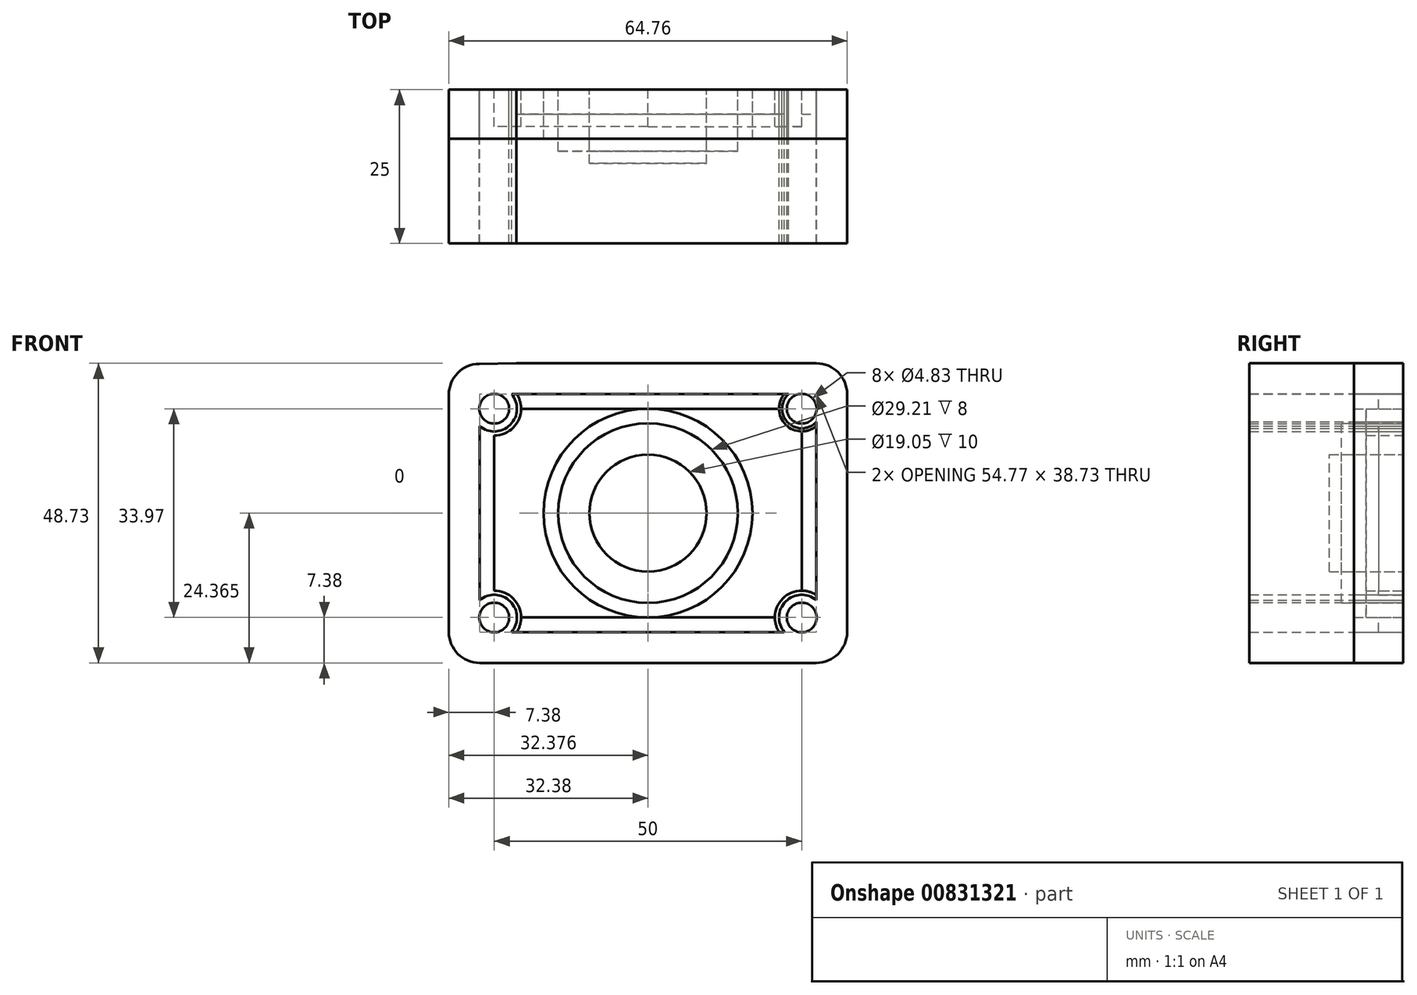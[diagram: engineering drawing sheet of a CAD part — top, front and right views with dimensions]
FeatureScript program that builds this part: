
annotation { "Feature Type Name" : "Feature", "Feature Type Description" : "" }
export const myFeature = defineFeature(function(context is Context, id is Id, definition is map)
    precondition{}
    {
        {
            var Q0;
            Q0=qCreatedBy(makeId("Front.planeOp"),FACE);
            var sketch = newSketch(context, id + "F0", { "sketchPlane" : qUnion([Q0])});
            skCircle(sketch, "E0", {"center": v(25, 0.52) * mm, "radius": 9.53 * mm});
            skCircle(sketch, "E1", {"center": v(25, 0.52) * mm, "radius": 14.6 * mm});
            skCircle(sketch, "E2", {"center": v(25, 0.52) * mm, "radius": 16.98 * mm});
            skLineSegment(sketch, "E3", {"start": v(25, 17.5) * mm, "end": v(46.8, 17.5) * mm});
            skLineSegment(sketch, "E4", {"start": v(25, 17.5) * mm, "end": v(4.37, 17.5) * mm});
            skLineSegment(sketch, "E5", {"start": v(25, -16.46) * mm, "end": v(46.31, -16.46) * mm});
            skLineSegment(sketch, "E6", {"start": v(25, -16.46) * mm, "end": v(3.69, -16.46) * mm});
            skLineSegment(sketch, "E7", {"start": v(50, 14.31) * mm, "end": v(50, -12.77) * mm});
            skLineSegment(sketch, "E8", {"start": v(0, -12.77) * mm, "end": v(0, 13.14) * mm});
            skLineSegment(sketch, "E9", {"start": v(-2.38, 17.5) * mm, "end": v(-2.38, 17.1) * mm});
            skLineSegment(sketch, "E10", {"start": v(-2.38, 17.5) * mm, "end": v(-2.38, 17.92) * mm});
            skLineSegment(sketch, "E11", {"start": v(-0.4, 19.89) * mm, "end": v(0.4, 19.89) * mm});
            skLineSegment(sketch, "E12", {"start": v(52.38, -16.46) * mm, "end": v(52.38, -16.87) * mm});
            skLineSegment(sketch, "E13", {"start": v(-2.38, -16.46) * mm, "end": v(-2.38, -16.87) * mm});
            skLineSegment(sketch, "E14", {"start": v(-0.4, -18.84) * mm, "end": v(0.4, -18.84) * mm});
            skCircle(sketch, "E15", {"center": v(0, -16.46) * mm, "radius": 2.42 * mm});
            skCircle(sketch, "E16", {"center": v(0, 17.5) * mm, "radius": 2.42 * mm});
            skCircle(sketch, "E17", {"center": v(50, 17.5) * mm, "radius": 2.42 * mm});
            skCircle(sketch, "E18", {"center": v(50, -16.46) * mm, "radius": 2.42 * mm});
            skArc(sketch, "E19", {"start": v(-2.38, 13.85) * mm, "mid": v(3.09, 14.42) * mm, "end": v(3.66, 19.89) * mm});
            skPoint(sketch, "E20.orphan", {"position": v(-2.38, 19.89) * mm});
            skLineSegment(sketch, "E21.trimOffspring", {"start": v(-2.38, 13.85) * mm, "end": v(-2.38, -13.64) * mm});
            skLineSegment(sketch, "E22", {"start": v(0, 0) * mm, "end": v(0, 10.6) * mm});
            skLineSegment(sketch, "E23", {"start": v(0, 0) * mm, "end": v(0, -10.6) * mm});
            skLineSegment(sketch, "E24.trimOffspring", {"start": v(4.37, 17.5) * mm, "end": v(6.92, 17.5) * mm});
            skLineSegment(sketch, "E25.trimOffspring", {"start": v(3.66, 19.89) * mm, "end": v(47.87, 19.89) * mm});
            skArc(sketch, "E26", {"start": v(-2.39, 14.7) * mm, "mid": v(2.6, 14.9) * mm, "end": v(2.82, 19.89) * mm});
            skLineSegment(sketch, "E27", {"start": v(2.82, 19.89) * mm, "end": v(4.36, 19.89) * mm});
            skLineSegment(sketch, "E28", {"start": v(-2.38, 13.85) * mm, "end": v(-2.39, 14.7) * mm});
            skArc(sketch, "E29", {"start": v(47.87, 19.89) * mm, "mid": v(47.74, 15.25) * mm, "end": v(52.38, 15.38) * mm});
            skArc(sketch, "E30", {"start": v(47.18, 19.89) * mm, "mid": v(47.4, 14.9) * mm, "end": v(52.38, 14.69) * mm});
            skLineSegment(sketch, "E31.trimOffspring", {"start": v(52.38, 15.38) * mm, "end": v(52.38, -13.64) * mm});
            skLineSegment(sketch, "E32", {"start": v(50, 19.92) * mm, "end": v(49.92, 19.92) * mm});
            skLineSegment(sketch, "E33", {"start": v(-7.38, 0) * mm, "end": v(-7.38, 19.81) * mm});
            skLineSegment(sketch, "E34", {"start": v(57.38, 0) * mm, "end": v(57.38, 19.89) * mm});
            skLineSegment(sketch, "E35", {"start": v(3.6, 24.89) * mm, "end": v(52.38, 24.89) * mm});
            skLineSegment(sketch, "E36", {"start": v(3.6, 24.89) * mm, "end": v(-2.45, 24.8) * mm});
            skLineSegment(sketch, "E37", {"start": v(-7.38, 23.87) * mm, "end": v(-7.4, 24.74) * mm});
            skLineSegment(sketch, "E38", {"start": v(52.38, -23.84) * mm, "end": v(52.38, -23.84) * mm});
            skLineSegment(sketch, "E39", {"start": v(57.38, -18.84) * mm, "end": v(57.38, 0) * mm});
            skLineSegment(sketch, "E40", {"start": v(-2.38, -23.84) * mm, "end": v(-2.38, -23.84) * mm});
            skLineSegment(sketch, "E41", {"start": v(-7.38, -18.84) * mm, "end": v(-7.38, -18.84) * mm});
            skLineSegment(sketch, "E42", {"start": v(-2.38, -23.84) * mm, "end": v(52.38, -23.84) * mm});
            skLineSegment(sketch, "E43", {"start": v(-7.38, -18.84) * mm, "end": v(-7.38, 0) * mm});
            skArc(sketch, "E44", {"start": v(2.82, -18.84) * mm, "mid": v(2.6, -13.85) * mm, "end": v(-2.38, -13.64) * mm});
            skArc(sketch, "E45", {"start": v(3.66, -18.84) * mm, "mid": v(3.09, -13.37) * mm, "end": v(-2.38, -12.8) * mm});
            skArc(sketch, "E46", {"start": v(52.38, -13.64) * mm, "mid": v(47.4, -13.85) * mm, "end": v(47.18, -18.84) * mm});
            skArc(sketch, "E47", {"start": v(52.38, -12.8) * mm, "mid": v(46.91, -13.37) * mm, "end": v(46.34, -18.84) * mm});
            skLineSegment(sketch, "E48.trimOffspring", {"start": v(52.38, -16.05) * mm, "end": v(52.38, -16.46) * mm});
            skLineSegment(sketch, "E49.trimOffspring", {"start": v(49.6, -18.84) * mm, "end": v(50.4, -18.84) * mm});
            skLineSegment(sketch, "E50.trimOffspring", {"start": v(2.82, -18.84) * mm, "end": v(47.18, -18.84) * mm});
            skLineSegment(sketch, "E51.trimOffspring", {"start": v(-2.38, -16.05) * mm, "end": v(-2.38, -16.46) * mm});
            skPoint(sketch, "E52.start.orphan", {"position": v(-2.38, 0) * mm});
            skPoint(sketch, "E53.start.orphan", {"position": v(52.38, 0) * mm});
            skArc(sketch, "E54.filletArc", {"start": v(-2.45, 24.8) * mm, "mid": v(-5.94, 23.32) * mm, "end": v(-7.38, 19.81) * mm});
            skPoint(sketch, "E55.visualSharp", {"position": v(57.38, 24.89) * mm});
            skArc(sketch, "E55.filletArc", {"start": v(57.38, 19.89) * mm, "mid": v(55.92, 23.42) * mm, "end": v(52.38, 24.89) * mm});
            skPoint(sketch, "E56.visualSharp", {"position": v(57.38, -23.84) * mm});
            skArc(sketch, "E56.filletArc", {"start": v(52.38, -23.84) * mm, "mid": v(55.92, -22.38) * mm, "end": v(57.38, -18.84) * mm});
            skPoint(sketch, "E57.visualSharp", {"position": v(-7.38, -23.84) * mm});
            skArc(sketch, "E57.filletArc", {"start": v(-7.38, -18.84) * mm, "mid": v(-5.92, -22.38) * mm, "end": v(-2.38, -23.84) * mm});
            skSolve(sketch);
        }
        {
            var Q0;
            Q0=makeQuery(id+"F0.imprint","IMPRINT",FACE,{"disambiguationData":[TD([[makeQuery(id+"F0.imprint","IMPRINT",EDGE,{"derivedFrom":sQuery(id+"F0.wireOp",EDGE,"E0")}),1.0]])]});
            extrude(context, id + "F1", {"entities" : qUnion([Q0]), "depth" : 12 * mm, "offsetDistance" : 25 * mm});
        }
        {
            var Q0;
            Q0 = qSketchRegion(id + "F0", true);
            extrude(context, id + "F2", {"entities" : qUnion([Q0]), "operationType" : NewBodyOperationType.ADD, "depth" : 25 * mm, "offsetDistance" : 25 * mm});
        }
        {
            var Q0;
            {var subQ9=sQuery(id+"F0.wireOp",EDGE,"E4");Q0=makeQuery(id+"F0.imprint","IMPRINT",FACE,{"disambiguationData":[TD([[makeQuery(id+"F0.imprint","IMPRINT",EDGE,{"derivedFrom":subQ9}),1.0]])]});}
            var Q1;
            {var subQ0=sQuery(id+"F0.wireOp",EDGE,"E30");var subQ1=sQuery(id+"F0.wireOp",EDGE,"E7");var subQ2=makeQuery(id+"F0.imprint","INTERSECT",VERTEX,{"derivedFrom":[subQ1,subQ0]});Q1=makeQuery(id+"F0.imprint","IMPRINT",FACE,{"disambiguationData":[TD([[makeQuery(id+"F0.imprint","IMPRINT",EDGE,{"disambiguationData":[TD([[subQ2,-1.0]])],"derivedFrom":subQ1}),-1.0]])]});}
            extrude(context, id + "F3", {"entities" : qUnion([Q0, Q1]), "depth" : 6 * mm, "offsetDistance" : 25 * mm});
        }
        {
            var Q0;
            Q0=makeQuery(id+"F0.imprint","IMPRINT",FACE,{"disambiguationData":[TD([[makeQuery(id+"F0.imprint","IMPRINT",EDGE,{"derivedFrom":sQuery(id+"F0.wireOp",EDGE,"E1")}),-1.0]])]});
            extrude(context, id + "F4", {"entities" : qUnion([Q0]), "depth" : 8 * mm, "offsetDistance" : 25 * mm});
        }
        {
            var Q0;
            Q0=makeQuery(id+"F0.imprint","IMPRINT",FACE,{"disambiguationData":[TD([[makeQuery(id+"F0.imprint","IMPRINT",EDGE,{"derivedFrom":sQuery(id+"F0.wireOp",EDGE,"E0")}),-1.0]])]});
            extrude(context, id + "F5", {"entities" : qUnion([Q0]), "depth" : 10 * mm, "offsetDistance" : 25 * mm});
        }
        {
            var Q0;
            {var subQ40=sQuery(id+"F0.wireOp",EDGE,"E26");Q0=makeQuery(id+"F0.imprint","IMPRINT",FACE,{"disambiguationData":[TD([[makeQuery(id+"F0.imprint","IMPRINT",EDGE,{"derivedFrom":subQ40}),1.0]])]});}
            extrude(context, id + "F6", {"entities" : qUnion([Q0]), "depth" : 8 * mm, "offsetDistance" : 25 * mm});
        }
        {
            var Q0;
            {var subQ0=sQuery(id+"F0.wireOp",EDGE,"E50.trimOffspring");var subQ5=sQuery(id+"F0.wireOp",EDGE,"E45");var subQ6=makeQuery(id+"F0.imprint","INTERSECT",VERTEX,{"derivedFrom":[subQ5,subQ0]});Q0=makeQuery(id+"F0.imprint","IMPRINT",FACE,{"disambiguationData":[TD([[makeQuery(id+"F0.imprint","IMPRINT",EDGE,{"disambiguationData":[TD([[subQ6,-1.0]])],"derivedFrom":subQ5}),-1.0]])]});}
            var Q1;
            {var subQ8=sQuery(id+"F0.wireOp",EDGE,"E22");Q1=makeQuery(id+"F0.imprint","IMPRINT",FACE,{"disambiguationData":[TD([[makeQuery(id+"F0.imprint","IMPRINT",EDGE,{"derivedFrom":subQ8}),1.0]])]});}
            var Q2;
            {var subQ0=sQuery(id+"F0.wireOp",EDGE,"E4");Q2=makeQuery(id+"F0.imprint","IMPRINT",FACE,{"disambiguationData":[TD([[makeQuery(id+"F0.imprint","IMPRINT",EDGE,{"derivedFrom":subQ0}),-1.0]])]});}
            var Q3;
            {var subQ0=sQuery(id+"F0.wireOp",EDGE,"E30");var subQ1=sQuery(id+"F0.wireOp",EDGE,"E7");var subQ2=makeQuery(id+"F0.imprint","INTERSECT",VERTEX,{"derivedFrom":[subQ1,subQ0]});Q3=makeQuery(id+"F0.imprint","IMPRINT",FACE,{"disambiguationData":[TD([[makeQuery(id+"F0.imprint","IMPRINT",EDGE,{"disambiguationData":[TD([[subQ2,-1.0]])],"derivedFrom":subQ1}),1.0]])]});}
            extrude(context, id + "F7", {"entities" : qUnion([Q0, Q1, Q2, Q3]), "depth" : 4 * mm, "offsetDistance" : 25 * mm});
        }
    });
